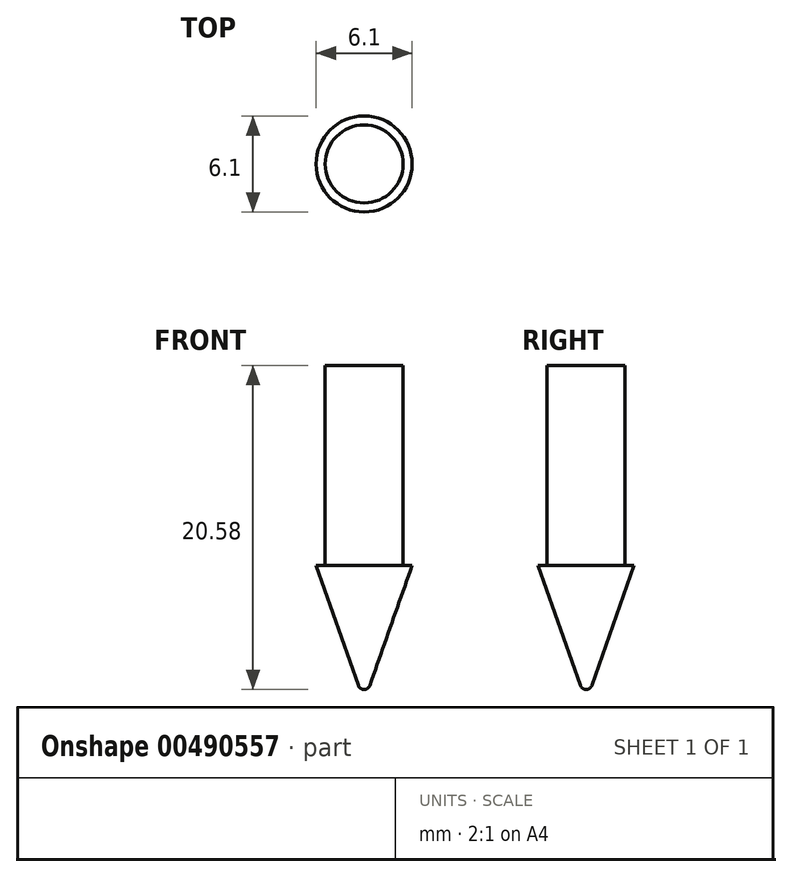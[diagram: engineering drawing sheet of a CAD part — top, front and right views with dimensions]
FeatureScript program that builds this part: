
annotation { "Feature Type Name" : "Feature", "Feature Type Description" : "" }
export const myFeature = defineFeature(function(context is Context, id is Id, definition is map)
    precondition{}
    {
        {
            var Q0;
            Q0=qCreatedBy(makeId("Front.planeOp"),FACE);
            var sketch = newSketch(context, id + "F0", { "sketchPlane" : qUnion([Q0])});
            skPoint(sketch, "E0.middle", {"position": v(0, 0) * mm});
            skLineSegment(sketch, "E1.bottom", {"start": v(0, 0) * mm, "end": v(-3.05, 0) * mm});
            skLineSegment(sketch, "E2", {"start": v(-3.05, 0) * mm, "end": v(-0.37, -7.62) * mm});
            skLineSegment(sketch, "E3.MirrorCS", {"start": v(3.05, 0) * mm, "end": v(0.37, -7.62) * mm});
            skLineSegment(sketch, "E4.MirrorCS", {"start": v(0, 0) * mm, "end": v(3.05, 0) * mm});
            skArc(sketch, "E5", {"start": v(-0.37, -7.62) * mm, "mid": v(0, -7.88) * mm, "end": v(0.37, -7.62) * mm});
            skLineSegment(sketch, "E6.top", {"start": v(-2.48, 12.7) * mm, "end": v(0, 12.7) * mm});
            skLineSegment(sketch, "E6.left", {"start": v(-2.48, 0) * mm, "end": v(-2.48, 12.7) * mm});
            skLineSegment(sketch, "E7.MirrorCS", {"start": v(2.48, 12.7) * mm, "end": v(0, 12.7) * mm});
            skLineSegment(sketch, "E8.MirrorCS", {"start": v(2.48, 0) * mm, "end": v(2.48, 12.7) * mm});
            skLineSegment(sketch, "E9", {"start": v(0, -7.5) * mm, "end": v(0, -7.88) * mm});
            skLineSegment(sketch, "E10", {"start": v(0, 12.7) * mm, "end": v(0, -7.88) * mm});
            skSolve(sketch);
        }
        {
            var Q0;
            {var subQ4=sQuery(id+"F0.wireOp",EDGE,"E6.top");Q0=makeQuery(id+"F0.imprint","IMPRINT",FACE,{"disambiguationData":[TD([[makeQuery(id+"F0.imprint","IMPRINT",EDGE,{"derivedFrom":subQ4}),-1.0]])]});}
            var Q1;
            {var subQ0=sQuery(id+"F0.wireOp",EDGE,"E2");Q1=makeQuery(id+"F0.imprint","IMPRINT",FACE,{"disambiguationData":[TD([[makeQuery(id+"F0.imprint","IMPRINT",EDGE,{"derivedFrom":subQ0}),1.0]])]});}
            var Q2;
            Q2=sQuery(id+"F0.wireOp",EDGE,"E10");
            revolve(context, id + "F1", {"entities" : qUnion([Q0, Q1]), "axis" : qUnion([Q2]), "revolveType" : RevolveType.FULL});
        }
    });
